# Revit family: Toilet_Universal-Floor_Mount-Sloan-ST-2449
name_source: partatom
category: Plumbing Fixtures
revit_build: Autodesk Revit 2014 (Build: 20130308_1515(x64)
units: mm (PartAtom-declared; Revit-internal decimal feet)

## types (1)
- ST-2449
    ADA Compliant = Yes
    Assembly Code = D2010110
    CW Connection = Yes
    CWFU = 10
    Default Elevation = 13 1/2"
    Description = Universal Floor Mounted TAS Compliant Vitreous China Water Closet
    Fixture Color = White
    Flush Volume = 1.1 to 1.6gpf/4.2 to 6.0Lpf
    HW Connection = No
    HWFU = 0
    High Efficiency = Yes
    IAPMO Certificate = cUPC
    Inlet Spud Size = 1-1/2" I.P.S. Top Spud Inlet
    Manufacturer = SLOAN
    Material = Vitreous China-Sloan-White
    Model = ST-2449
    Mounting = Floor Mount
    Order Code = 2102449
    Price = Prices may vary. Please consult Sloan Rep for most up-to-date price list.
    Revision Date = 1/23/2017
    Spud Inlet Radius = 3/4"
    Spud Location = Top Spud
    TAS Compliant = Yes
    URL = https://www.sloan.com
    Vent Connection = No
    WFU = 10
    Waste Connection = Yes
    Waste Connection Radius = 1 1/16"

## geometry (parser evidence)
native form markers: Sweep x1
no freeform markers — native parametric forms only
